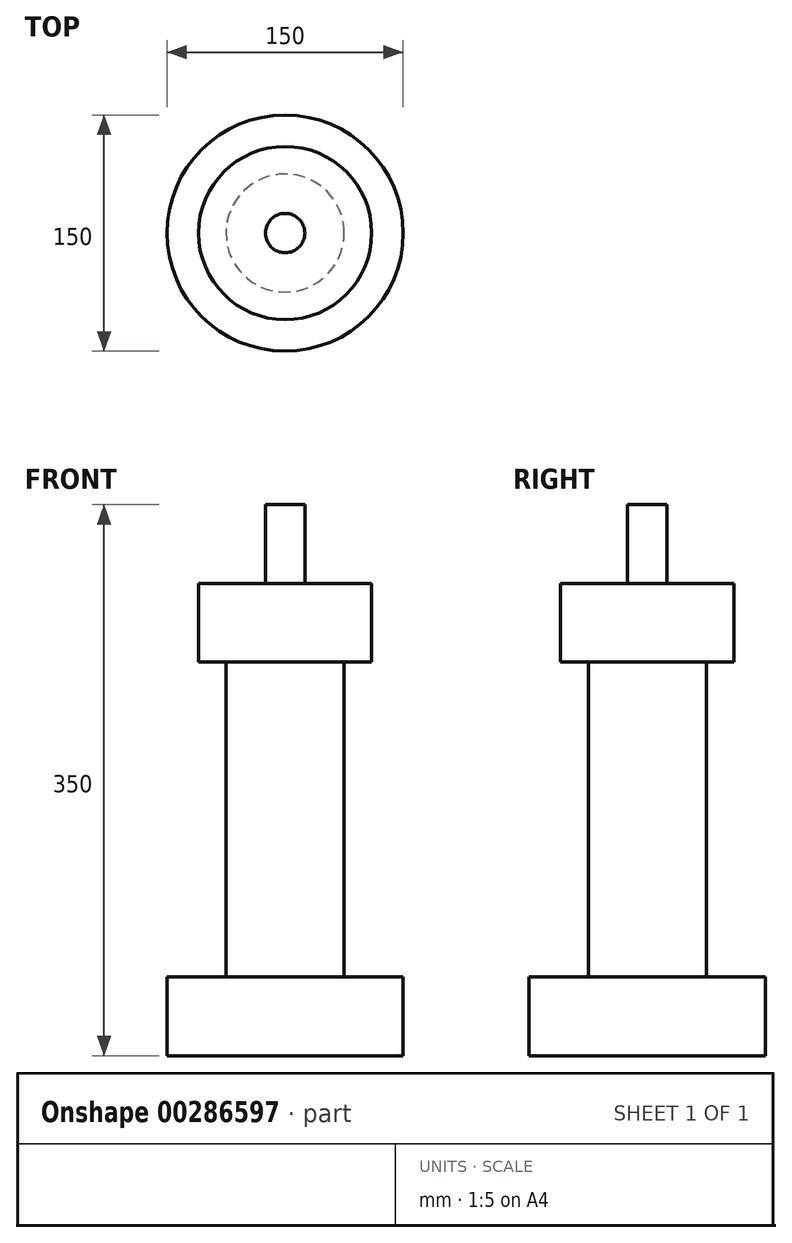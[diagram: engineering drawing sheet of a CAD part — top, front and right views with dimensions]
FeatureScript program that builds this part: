
annotation { "Feature Type Name" : "Feature", "Feature Type Description" : "" }
export const myFeature = defineFeature(function(context is Context, id is Id, definition is map)
    precondition{}
    {
        {
            var Q0;
            Q0=qCreatedBy(makeId("Top.planeOp"),FACE);
            var sketch = newSketch(context, id + "F0", { "sketchPlane" : qUnion([Q0])});
            skCircle(sketch, "E0", {"center": v(0, 0) * mm, "radius": 75 * mm});
            skSolve(sketch);
        }
        {
            var Q0;
            Q0=makeQuery(id+"F0.imprint","IMPRINT",FACE,{"disambiguationData":[TD([[makeQuery(id+"F0.imprint","IMPRINT",EDGE,{"derivedFrom":sQuery(id+"F0.wireOp",EDGE,"E0")}),1.0]])]});
            extrude(context, id + "F1", {"entities" : qUnion([Q0]), "depth" : 50 * mm});
        }
        {
            var Q0;
            Q0=makeQuery(id+"F1.opExtrude","CAP_FACE",FACE,{"disambiguationData":[OSD([sQuery(id+"F0.wireOp",EDGE,"E0")])],"isStart":false});
            var sketch = newSketch(context, id + "F2", { "sketchPlane" : qUnion([Q0])});
            skCircle(sketch, "E1", {"center": v(0, 0) * mm, "radius": 37.5 * mm});
            skSolve(sketch);
        }
        {
            var Q0;
            Q0=makeQuery(id+"F2.imprint","IMPRINT",FACE,{"disambiguationData":[TD([[makeQuery(id+"F2.imprint","IMPRINT",EDGE,{"derivedFrom":sQuery(id+"F2.wireOp",EDGE,"E1")}),1.0]])]});
            extrude(context, id + "F3", {"entities" : qUnion([Q0]), "operationType" : NewBodyOperationType.ADD, "depth" : 200 * mm});
        }
        {
            var Q0;
            Q0=makeQuery(id+"F3.opExtrude","CAP_FACE",FACE,{"disambiguationData":[OSD([sQuery(id+"F2.wireOp",EDGE,"E1")])],"isStart":false});
            var sketch = newSketch(context, id + "F4", { "sketchPlane" : qUnion([Q0])});
            skCircle(sketch, "E2", {"center": v(0, 0) * mm, "radius": 55 * mm});
            skSolve(sketch);
        }
        {
            var Q0;
            Q0=makeQuery(id+"F4.imprint","IMPRINT",FACE,{"disambiguationData":[TD([[makeQuery(id+"F4.imprint","IMPRINT",EDGE,{"derivedFrom":makeQuery(id+"F3.opExtrude","CAP_EDGE",EDGE,{"disambiguationData":[OSD([sQuery(id+"F2.wireOp",EDGE,"E1")])],"isStart":false})}),1.0]])]});
            var Q1;
            Q1=makeQuery(id+"F4.imprint","IMPRINT",FACE,{"disambiguationData":[TD([[makeQuery(id+"F4.imprint","IMPRINT",EDGE,{"derivedFrom":sQuery(id+"F4.wireOp",EDGE,"E2")}),1.0]])]});
            extrude(context, id + "F5", {"entities" : qUnion([Q0, Q1]), "operationType" : NewBodyOperationType.ADD, "depth" : 50 * mm});
        }
        {
            var Q0;
            Q0=makeQuery(id+"F5.opExtrude","CAP_FACE",FACE,{"disambiguationData":[OSD([sQuery(id+"F4.wireOp",EDGE,"E2")])],"isStart":false});
            var sketch = newSketch(context, id + "F6", { "sketchPlane" : qUnion([Q0])});
            skCircle(sketch, "E3", {"center": v(0, 0) * mm, "radius": 12.5 * mm});
            skSolve(sketch);
        }
        {
            var Q0;
            Q0=makeQuery(id+"F6.imprint","IMPRINT",FACE,{"disambiguationData":[TD([[makeQuery(id+"F6.imprint","IMPRINT",EDGE,{"derivedFrom":sQuery(id+"F6.wireOp",EDGE,"E3")}),1.0]])]});
            extrude(context, id + "F7", {"entities" : qUnion([Q0]), "operationType" : NewBodyOperationType.ADD, "depth" : 50 * mm});
        }
    });
